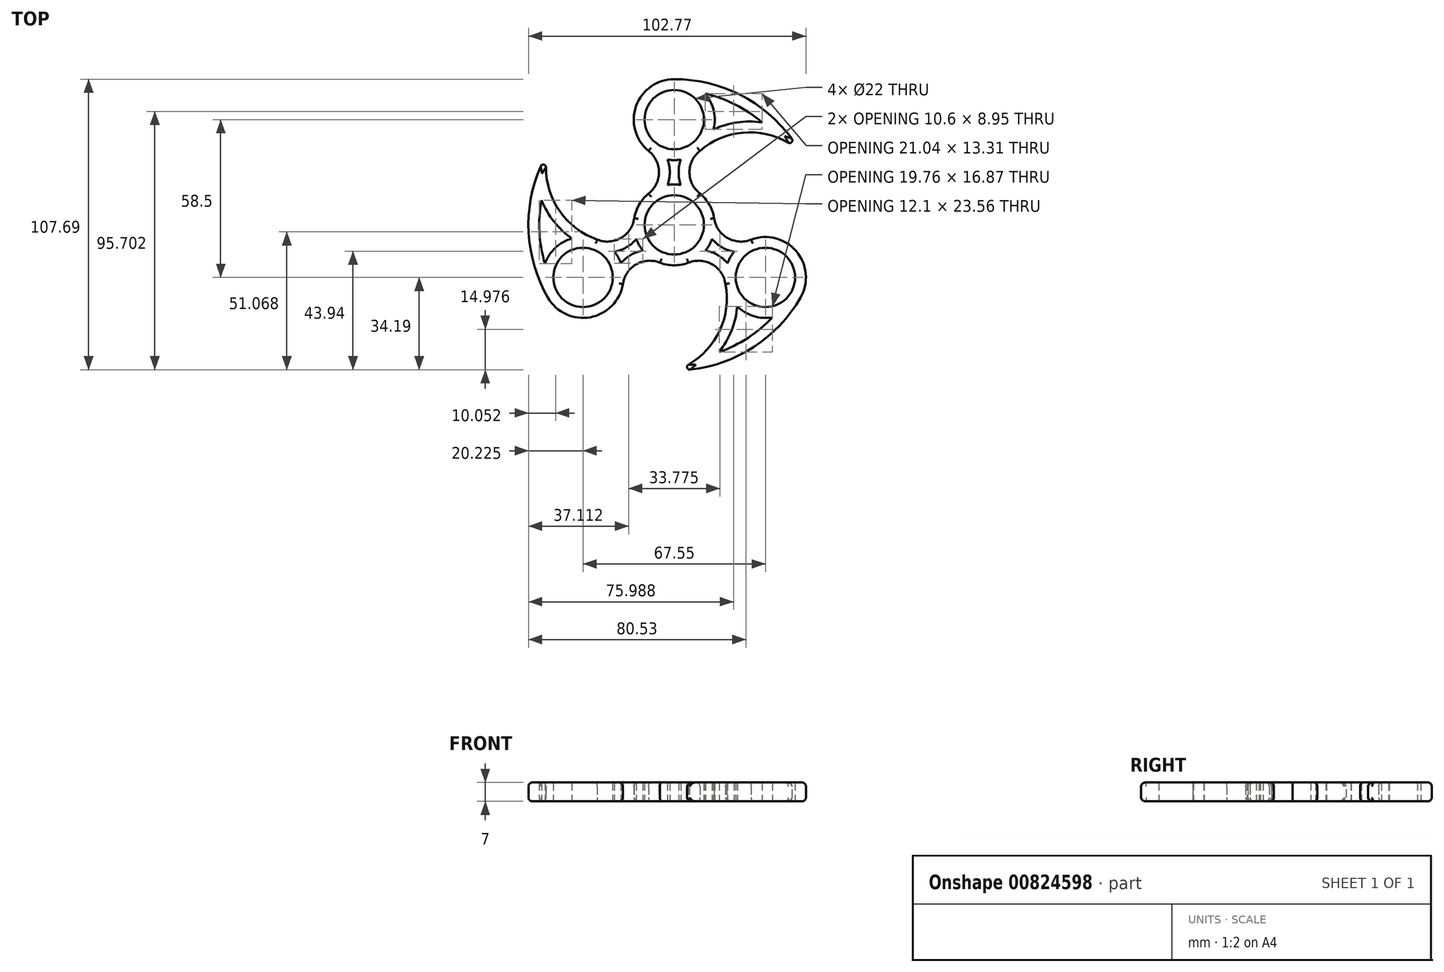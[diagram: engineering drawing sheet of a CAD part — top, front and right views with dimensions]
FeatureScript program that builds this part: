
annotation { "Feature Type Name" : "Feature", "Feature Type Description" : "" }
export const myFeature = defineFeature(function(context is Context, id is Id, definition is map)
    precondition{}
    {
        {
            var Q0;
            Q0=qCreatedBy(makeId("Top.planeOp"),FACE);
            var sketch = newSketch(context, id + "F0", { "sketchPlane" : qUnion([Q0])});
            skCircle(sketch, "E0", {"center": v(0, 0) * mm, "radius": 11 * mm});
            skCircle(sketch, "E1", {"center": v(0, 0) * mm, "radius": 15 * mm});
            skCircle(sketch, "E2", {"center": v(0, 39) * mm, "radius": 11 * mm});
            skCircle(sketch, "E3", {"center": v(0, 39) * mm, "radius": 15 * mm});
            skPoint(sketch, "E4", {"position": v(9.52, 27.4) * mm});
            skPoint(sketch, "E5", {"position": v(9.52, 11.6) * mm});
            skArc(sketch, "E6", {"start": v(9.52, 27.4) * mm, "mid": v(5.64, 19.5) * mm, "end": v(9.52, 11.6) * mm});
            skArc(sketch, "E7.MirrorCS", {"start": v(-9.52, 27.4) * mm, "mid": v(-5.64, 19.5) * mm, "end": v(-9.52, 11.6) * mm});
            skPoint(sketch, "E8", {"position": v(0, 54) * mm});
            skArc(sketch, "E9", {"start": v(46.53, 27.4) * mm, "mid": v(28.02, 34.3) * mm, "end": v(9.52, 27.4) * mm});
            skArc(sketch, "E10", {"start": v(46.53, 27.4) * mm, "mid": v(26.8, 46.88) * mm, "end": v(0, 54) * mm});
            skArc(sketch, "E11.0", {"start": v(32.5, 38) * mm, "mid": v(18.88, 36.98) * mm, "end": v(6.9, 30.43) * mm});
            skArc(sketch, "E11.1", {"start": v(32.5, 38) * mm, "mid": v(17.33, 46.9) * mm, "end": v(0, 50) * mm});
            skCircle(sketch, "E12.1.0", {"center": v(-33.77, -19.5) * mm, "radius": 11 * mm});
            skArc(sketch, "E12.1.1", {"start": v(-49.15, 9.16) * mm, "mid": v(-49.28, -8.45) * mm, "end": v(-43.3, -25) * mm});
            skArc(sketch, "E12.1.2", {"start": v(-49.15, 9.16) * mm, "mid": v(-41.47, -2.14) * mm, "end": v(-29.8, -9.24) * mm});
            skArc(sketch, "E12.1.3", {"start": v(-47, 26.6) * mm, "mid": v(-54, -0.23) * mm, "end": v(-46.77, -27) * mm});
            skArc(sketch, "E12.1.4", {"start": v(-47, 26.6) * mm, "mid": v(-43.72, 7.12) * mm, "end": v(-28.5, -5.46) * mm});
            skArc(sketch, "E12.1.5", {"start": v(-18.98, -21.94) * mm, "mid": v(-14.07, -14.64) * mm, "end": v(-5.28, -14.04) * mm});
            skArc(sketch, "E12.1.6", {"start": v(-28.5, -5.46) * mm, "mid": v(-19.7, -4.86) * mm, "end": v(-14.8, 2.44) * mm});
            skCircle(sketch, "E12.1.7", {"center": v(-33.77, -19.5) * mm, "radius": 15 * mm});
            skPoint(sketch, "E12.1.10", {"position": v(-46.77, -27) * mm});
            skPoint(sketch, "E12.1.11", {"position": v(-28.5, -5.46) * mm});
            skCircle(sketch, "E12.2.0", {"center": v(33.77, -19.5) * mm, "radius": 11 * mm});
            skArc(sketch, "E12.2.1", {"start": v(16.65, -47.15) * mm, "mid": v(31.95, -38.46) * mm, "end": v(43.3, -25) * mm});
            skArc(sketch, "E12.2.2", {"start": v(16.65, -47.15) * mm, "mid": v(22.59, -34.84) * mm, "end": v(22.9, -21.19) * mm});
            skArc(sketch, "E12.2.3", {"start": v(0.47, -54) * mm, "mid": v(27.2, -46.65) * mm, "end": v(46.77, -27) * mm});
            skArc(sketch, "E12.2.4", {"start": v(0.47, -54) * mm, "mid": v(15.7, -41.42) * mm, "end": v(18.98, -21.94) * mm});
            skArc(sketch, "E12.2.5", {"start": v(28.5, -5.46) * mm, "mid": v(19.7, -4.86) * mm, "end": v(14.8, 2.44) * mm});
            skArc(sketch, "E12.2.6", {"start": v(18.98, -21.94) * mm, "mid": v(14.07, -14.64) * mm, "end": v(5.28, -14.04) * mm});
            skCircle(sketch, "E12.2.7", {"center": v(33.77, -19.5) * mm, "radius": 15 * mm});
            skPoint(sketch, "E12.2.10", {"position": v(46.77, -27) * mm});
            skPoint(sketch, "E12.2.11", {"position": v(18.98, -21.94) * mm});
            skArc(sketch, "E13.0", {"start": v(7.07, 30.57) * mm, "mid": v(1.64, 19.5) * mm, "end": v(7.07, 8.43) * mm});
            skArc(sketch, "E14.0", {"start": v(-7.07, 30.57) * mm, "mid": v(-1.64, 19.5) * mm, "end": v(-7.07, 8.43) * mm});
            skArc(sketch, "E15.1.0", {"start": v(-22.94, -21.4) * mm, "mid": v(-16.07, -11.17) * mm, "end": v(-3.77, -10.34) * mm});
            skArc(sketch, "E15.1.1", {"start": v(-30, -9.16) * mm, "mid": v(-17.7, -8.33) * mm, "end": v(-10.84, 1.9) * mm});
            skArc(sketch, "E15.2.0", {"start": v(30, -9.16) * mm, "mid": v(17.7, -8.33) * mm, "end": v(10.84, 1.9) * mm});
            skArc(sketch, "E15.2.1", {"start": v(22.94, -21.4) * mm, "mid": v(16.07, -11.17) * mm, "end": v(3.77, -10.34) * mm});
            skSolve(sketch);
        }
        {
            var Q0;
            {var subQ0=sQuery(id+"F0.wireOp",EDGE,"E10");Q0=makeQuery(id+"F0.imprint","IMPRINT",FACE,{"disambiguationData":[TD([[makeQuery(id+"F0.imprint","IMPRINT",EDGE,{"derivedFrom":subQ0}),1.0]])]});}
            var Q1;
            {var subQ4=sQuery(id+"F0.wireOp",EDGE,"E11.1");var subQ7=sQuery(id+"F0.wireOp",EDGE,"E2");var subQ10=makeQuery(id+"F0.imprint","INTERSECT",VERTEX,{"derivedFrom":[subQ7,subQ4]});Q1=makeQuery(id+"F0.imprint","IMPRINT",FACE,{"disambiguationData":[TD([[makeQuery(id+"F0.imprint","IMPRINT",EDGE,{"disambiguationData":[TD([[subQ10,-1.0]])],"derivedFrom":subQ7}),-1.0]])]});}
            var Q2;
            {var subQ0=sQuery(id+"F0.wireOp",EDGE,"E11.1");var subQ1=sQuery(id+"F0.wireOp",EDGE,"E2");var subQ2=makeQuery(id+"F0.imprint","INTERSECT",VERTEX,{"derivedFrom":[subQ1,subQ0]});Q2=makeQuery(id+"F0.imprint","IMPRINT",FACE,{"disambiguationData":[TD([[makeQuery(id+"F0.imprint","IMPRINT",EDGE,{"disambiguationData":[TD([[subQ2,1.0]])],"derivedFrom":subQ1}),-1.0]])]});}
            var Q3;
            {var subQ5=sQuery(id+"F0.wireOp",EDGE,"E2");var subQ7=sQuery(id+"F0.wireOp",EDGE,"E11.0");var subQ10=makeQuery(id+"F0.imprint","INTERSECT",VERTEX,{"disambiguationData":[OD(0.0)],"derivedFrom":[subQ5,subQ7]});Q3=makeQuery(id+"F0.imprint","IMPRINT",FACE,{"disambiguationData":[TD([[makeQuery(id+"F0.imprint","IMPRINT",EDGE,{"disambiguationData":[TD([[subQ10,1.0]])],"derivedFrom":subQ5}),-1.0]])]});}
            var Q4;
            {var subQ0=sQuery(id+"F0.wireOp",EDGE,"E14.0");var subQ1=sQuery(id+"F0.wireOp",EDGE,"E2");var subQ2=makeQuery(id+"F0.imprint","INTERSECT",VERTEX,{"disambiguationData":[OD(1.0)],"derivedFrom":[subQ1,subQ0]});Q4=makeQuery(id+"F0.imprint","IMPRINT",FACE,{"disambiguationData":[TD([[makeQuery(id+"F0.imprint","IMPRINT",EDGE,{"disambiguationData":[TD([[subQ2,-1.0]])],"derivedFrom":subQ1}),-1.0]])]});}
            var Q5;
            {var subQ0=sQuery(id+"F0.wireOp",EDGE,"E6");var subQ1=sQuery(id+"F0.wireOp",EDGE,"E1");var subQ2=makeQuery(id+"F0.imprint","INTERSECT",VERTEX,{"disambiguationData":[OD(1.0)],"derivedFrom":[subQ1,subQ0]});Q5=makeQuery(id+"F0.imprint","IMPRINT",FACE,{"disambiguationData":[TD([[makeQuery(id+"F0.imprint","IMPRINT",EDGE,{"disambiguationData":[TD([[subQ2,-1.0]])],"derivedFrom":subQ1}),-1.0]])]});}
            var Q6;
            {var subQ0=sQuery(id+"F0.wireOp",EDGE,"E7.MirrorCS");var subQ1=sQuery(id+"F0.wireOp",EDGE,"E1");var subQ2=makeQuery(id+"F0.imprint","INTERSECT",VERTEX,{"disambiguationData":[OD(1.0)],"derivedFrom":[subQ1,subQ0]});Q6=makeQuery(id+"F0.imprint","IMPRINT",FACE,{"disambiguationData":[TD([[makeQuery(id+"F0.imprint","IMPRINT",EDGE,{"disambiguationData":[TD([[subQ2,1.0]])],"derivedFrom":subQ1}),-1.0]])]});}
            var Q7;
            {var subQ3=sQuery(id+"F0.wireOp",EDGE,"E14.0");var subQ6=sQuery(id+"F0.wireOp",EDGE,"E0");var subQ12=makeQuery(id+"F0.imprint","INTERSECT",VERTEX,{"disambiguationData":[OD(0.0)],"derivedFrom":[subQ6,subQ3]});Q7=makeQuery(id+"F0.imprint","IMPRINT",FACE,{"disambiguationData":[TD([[makeQuery(id+"F0.imprint","IMPRINT",EDGE,{"disambiguationData":[TD([[subQ12,1.0]])],"derivedFrom":subQ6}),-1.0]])]});}
            var Q8;
            {var subQ0=sQuery(id+"F0.wireOp",EDGE,"E15.1.1");var subQ1=sQuery(id+"F0.wireOp",EDGE,"E0");var subQ2=makeQuery(id+"F0.imprint","INTERSECT",VERTEX,{"disambiguationData":[OD(1.0)],"derivedFrom":[subQ1,subQ0]});Q8=makeQuery(id+"F0.imprint","IMPRINT",FACE,{"disambiguationData":[TD([[makeQuery(id+"F0.imprint","IMPRINT",EDGE,{"disambiguationData":[TD([[subQ2,-1.0]])],"derivedFrom":subQ1}),-1.0]])]});}
            var Q9;
            {var subQ1=sQuery(id+"F0.wireOp",EDGE,"E0");var subQ4=sQuery(id+"F0.wireOp",EDGE,"E15.1.0");var subQ5=makeQuery(id+"F0.imprint","INTERSECT",VERTEX,{"disambiguationData":[OD(0.0)],"derivedFrom":[subQ1,subQ4]});Q9=makeQuery(id+"F0.imprint","IMPRINT",FACE,{"disambiguationData":[TD([[makeQuery(id+"F0.imprint","IMPRINT",EDGE,{"disambiguationData":[TD([[subQ5,1.0]])],"derivedFrom":subQ1}),-1.0]])]});}
            var Q10;
            {var subQ0=sQuery(id+"F0.wireOp",EDGE,"E15.2.0");var subQ1=sQuery(id+"F0.wireOp",EDGE,"E0");var subQ2=makeQuery(id+"F0.imprint","INTERSECT",VERTEX,{"disambiguationData":[OD(1.0)],"derivedFrom":[subQ1,subQ0]});Q10=makeQuery(id+"F0.imprint","IMPRINT",FACE,{"disambiguationData":[TD([[makeQuery(id+"F0.imprint","IMPRINT",EDGE,{"disambiguationData":[TD([[subQ2,1.0]])],"derivedFrom":subQ1}),-1.0]])]});}
            var Q11;
            {var subQ6=sQuery(id+"F0.wireOp",EDGE,"E0");var subQ10=sQuery(id+"F0.wireOp",EDGE,"E15.2.0");var subQ11=makeQuery(id+"F0.imprint","INTERSECT",VERTEX,{"disambiguationData":[OD(0.0)],"derivedFrom":[subQ6,subQ10]});Q11=makeQuery(id+"F0.imprint","IMPRINT",FACE,{"disambiguationData":[TD([[makeQuery(id+"F0.imprint","IMPRINT",EDGE,{"disambiguationData":[TD([[subQ11,1.0]])],"derivedFrom":subQ6}),-1.0]])]});}
            var Q12;
            {var subQ0=sQuery(id+"F0.wireOp",EDGE,"E13.0");var subQ1=sQuery(id+"F0.wireOp",EDGE,"E0");var subQ2=makeQuery(id+"F0.imprint","INTERSECT",VERTEX,{"disambiguationData":[OD(1.0)],"derivedFrom":[subQ1,subQ0]});Q12=makeQuery(id+"F0.imprint","IMPRINT",FACE,{"disambiguationData":[TD([[makeQuery(id+"F0.imprint","IMPRINT",EDGE,{"disambiguationData":[TD([[subQ2,-1.0]])],"derivedFrom":subQ1}),-1.0]])]});}
            var Q13;
            {var subQ0=sQuery(id+"F0.wireOp",EDGE,"E12.2.5");var subQ1=sQuery(id+"F0.wireOp",EDGE,"E1");var subQ2=makeQuery(id+"F0.imprint","INTERSECT",VERTEX,{"disambiguationData":[OD(1.0)],"derivedFrom":[subQ1,subQ0]});Q13=makeQuery(id+"F0.imprint","IMPRINT",FACE,{"disambiguationData":[TD([[makeQuery(id+"F0.imprint","IMPRINT",EDGE,{"disambiguationData":[TD([[subQ2,1.0]])],"derivedFrom":subQ1}),-1.0]])]});}
            var Q14;
            {var subQ0=sQuery(id+"F0.wireOp",EDGE,"E12.2.6");var subQ1=sQuery(id+"F0.wireOp",EDGE,"E1");var subQ2=makeQuery(id+"F0.imprint","INTERSECT",VERTEX,{"disambiguationData":[OD(1.0)],"derivedFrom":[subQ1,subQ0]});Q14=makeQuery(id+"F0.imprint","IMPRINT",FACE,{"disambiguationData":[TD([[makeQuery(id+"F0.imprint","IMPRINT",EDGE,{"disambiguationData":[TD([[subQ2,-1.0]])],"derivedFrom":subQ1}),-1.0]])]});}
            var Q15;
            {var subQ0=sQuery(id+"F0.wireOp",EDGE,"E12.2.2");var subQ1=sQuery(id+"F0.wireOp",EDGE,"E12.2.0");var subQ10=makeQuery(id+"F0.imprint","INTERSECT",VERTEX,{"disambiguationData":[OD(0.0)],"derivedFrom":[subQ1,subQ0]});Q15=makeQuery(id+"F0.imprint","IMPRINT",FACE,{"disambiguationData":[TD([[makeQuery(id+"F0.imprint","IMPRINT",EDGE,{"disambiguationData":[TD([[subQ10,1.0]])],"derivedFrom":subQ1}),-1.0]])]});}
            var Q16;
            {var subQ0=sQuery(id+"F0.wireOp",EDGE,"E12.2.3");Q16=makeQuery(id+"F0.imprint","IMPRINT",FACE,{"disambiguationData":[TD([[makeQuery(id+"F0.imprint","IMPRINT",EDGE,{"derivedFrom":subQ0}),1.0]])]});}
            var Q17;
            {var subQ0=sQuery(id+"F0.wireOp",EDGE,"E12.2.1");var subQ1=sQuery(id+"F0.wireOp",EDGE,"E12.2.0");var subQ2=makeQuery(id+"F0.imprint","INTERSECT",VERTEX,{"derivedFrom":[subQ1,subQ0]});Q17=makeQuery(id+"F0.imprint","IMPRINT",FACE,{"disambiguationData":[TD([[makeQuery(id+"F0.imprint","IMPRINT",EDGE,{"disambiguationData":[TD([[subQ2,1.0]])],"derivedFrom":subQ1}),-1.0]])]});}
            var Q18;
            {var subQ0=sQuery(id+"F0.wireOp",EDGE,"E12.2.1");var subQ1=sQuery(id+"F0.wireOp",EDGE,"E12.2.0");var subQ2=makeQuery(id+"F0.imprint","INTERSECT",VERTEX,{"derivedFrom":[subQ1,subQ0]});Q18=makeQuery(id+"F0.imprint","IMPRINT",FACE,{"disambiguationData":[TD([[makeQuery(id+"F0.imprint","IMPRINT",EDGE,{"disambiguationData":[TD([[subQ2,-1.0]])],"derivedFrom":subQ1}),-1.0]])]});}
            var Q19;
            {var subQ0=sQuery(id+"F0.wireOp",EDGE,"E15.2.0");var subQ1=sQuery(id+"F0.wireOp",EDGE,"E12.2.0");var subQ2=makeQuery(id+"F0.imprint","INTERSECT",VERTEX,{"disambiguationData":[OD(1.0)],"derivedFrom":[subQ1,subQ0]});Q19=makeQuery(id+"F0.imprint","IMPRINT",FACE,{"disambiguationData":[TD([[makeQuery(id+"F0.imprint","IMPRINT",EDGE,{"disambiguationData":[TD([[subQ2,-1.0]])],"derivedFrom":subQ1}),-1.0]])]});}
            var Q20;
            {var subQ0=sQuery(id+"F0.wireOp",EDGE,"E12.1.5");var subQ1=sQuery(id+"F0.wireOp",EDGE,"E1");var subQ2=makeQuery(id+"F0.imprint","INTERSECT",VERTEX,{"disambiguationData":[OD(1.0)],"derivedFrom":[subQ1,subQ0]});Q20=makeQuery(id+"F0.imprint","IMPRINT",FACE,{"disambiguationData":[TD([[makeQuery(id+"F0.imprint","IMPRINT",EDGE,{"disambiguationData":[TD([[subQ2,1.0]])],"derivedFrom":subQ1}),-1.0]])]});}
            var Q21;
            {var subQ0=sQuery(id+"F0.wireOp",EDGE,"E12.1.6");var subQ1=sQuery(id+"F0.wireOp",EDGE,"E1");var subQ2=makeQuery(id+"F0.imprint","INTERSECT",VERTEX,{"disambiguationData":[OD(1.0)],"derivedFrom":[subQ1,subQ0]});Q21=makeQuery(id+"F0.imprint","IMPRINT",FACE,{"disambiguationData":[TD([[makeQuery(id+"F0.imprint","IMPRINT",EDGE,{"disambiguationData":[TD([[subQ2,-1.0]])],"derivedFrom":subQ1}),-1.0]])]});}
            var Q22;
            {var subQ0=sQuery(id+"F0.wireOp",EDGE,"E12.1.2");var subQ1=sQuery(id+"F0.wireOp",EDGE,"E12.1.0");var subQ11=makeQuery(id+"F0.imprint","INTERSECT",VERTEX,{"disambiguationData":[OD(0.0)],"derivedFrom":[subQ1,subQ0]});Q22=makeQuery(id+"F0.imprint","IMPRINT",FACE,{"disambiguationData":[TD([[makeQuery(id+"F0.imprint","IMPRINT",EDGE,{"disambiguationData":[TD([[subQ11,1.0]])],"derivedFrom":subQ1}),-1.0]])]});}
            var Q23;
            {var subQ0=sQuery(id+"F0.wireOp",EDGE,"E15.1.0");var subQ1=sQuery(id+"F0.wireOp",EDGE,"E12.1.0");var subQ2=makeQuery(id+"F0.imprint","INTERSECT",VERTEX,{"disambiguationData":[OD(1.0)],"derivedFrom":[subQ1,subQ0]});Q23=makeQuery(id+"F0.imprint","IMPRINT",FACE,{"disambiguationData":[TD([[makeQuery(id+"F0.imprint","IMPRINT",EDGE,{"disambiguationData":[TD([[subQ2,-1.0]])],"derivedFrom":subQ1}),-1.0]])]});}
            var Q24;
            {var subQ0=sQuery(id+"F0.wireOp",EDGE,"E12.1.1");var subQ1=sQuery(id+"F0.wireOp",EDGE,"E12.1.0");var subQ2=makeQuery(id+"F0.imprint","INTERSECT",VERTEX,{"derivedFrom":[subQ1,subQ0]});Q24=makeQuery(id+"F0.imprint","IMPRINT",FACE,{"disambiguationData":[TD([[makeQuery(id+"F0.imprint","IMPRINT",EDGE,{"disambiguationData":[TD([[subQ2,-1.0]])],"derivedFrom":subQ1}),-1.0]])]});}
            var Q25;
            {var subQ0=sQuery(id+"F0.wireOp",EDGE,"E12.1.1");var subQ1=sQuery(id+"F0.wireOp",EDGE,"E12.1.0");var subQ2=makeQuery(id+"F0.imprint","INTERSECT",VERTEX,{"derivedFrom":[subQ1,subQ0]});Q25=makeQuery(id+"F0.imprint","IMPRINT",FACE,{"disambiguationData":[TD([[makeQuery(id+"F0.imprint","IMPRINT",EDGE,{"disambiguationData":[TD([[subQ2,1.0]])],"derivedFrom":subQ1}),-1.0]])]});}
            var Q26;
            {var subQ0=sQuery(id+"F0.wireOp",EDGE,"E12.1.3");Q26=makeQuery(id+"F0.imprint","IMPRINT",FACE,{"disambiguationData":[TD([[makeQuery(id+"F0.imprint","IMPRINT",EDGE,{"derivedFrom":subQ0}),1.0]])]});}
            extrude(context, id + "F1", {"entities" : qUnion([Q0, Q1, Q2, Q3, Q4, Q5, Q6, Q7, Q8, Q9, Q10, Q11, Q12, Q13, Q14, Q15, Q16, Q17, Q18, Q19, Q20, Q21, Q22, Q23, Q24, Q25, Q26]), "depth" : 7 * mm, "offsetDistance" : 25 * mm});
        }
        {
            var Q0;
            Q0=makeQuery(id+"F1.opExtrude","CAP_EDGE",EDGE,{"disambiguationData":[OSD([sQuery(id+"F0.wireOp",EDGE,"E10")])],"isStart":false});
            var Q1;
            {var subQ0=sQuery(id+"F0.wireOp",EDGE,"E3");Q1=makeQuery(id+"F1.opExtrude","CAP_EDGE",EDGE,{"disambiguationData":[OSD([subQ0]),TDD([makeQuery(id+"F0.imprint","IMPRINT",EDGE,{"disambiguationData":[TD([[makeQuery(id+"F0.imprint","INTERSECT",VERTEX,{"disambiguationData":[OD(0.0)],"derivedFrom":[subQ0,sQuery(id+"F0.wireOp",EDGE,"E7.MirrorCS")]}),1.0]])],"derivedFrom":subQ0})])],"isStart":false});}
            var Q2;
            Q2=makeQuery(id+"F1.opExtrude","CAP_EDGE",EDGE,{"disambiguationData":[OSD([sQuery(id+"F0.wireOp",EDGE,"E7.MirrorCS")])],"isStart":false});
            var Q3;
            {var subQ0=sQuery(id+"F0.wireOp",EDGE,"E1");Q3=makeQuery(id+"F1.opExtrude","CAP_EDGE",EDGE,{"disambiguationData":[OSD([subQ0]),TDD([makeQuery(id+"F0.imprint","IMPRINT",EDGE,{"disambiguationData":[TD([[makeQuery(id+"F0.imprint","INTERSECT",VERTEX,{"disambiguationData":[OD(0.0)],"derivedFrom":[subQ0,sQuery(id+"F0.wireOp",EDGE,"E7.MirrorCS")]}),-1.0]])],"derivedFrom":subQ0})])],"isStart":false});}
            var Q4;
            Q4=makeQuery(id+"F1.opExtrude","CAP_EDGE",EDGE,{"disambiguationData":[OSD([sQuery(id+"F0.wireOp",EDGE,"E12.1.6")])],"isStart":false});
            var Q5;
            Q5=makeQuery(id+"F1.opExtrude","CAP_EDGE",EDGE,{"disambiguationData":[OSD([sQuery(id+"F0.wireOp",EDGE,"E12.1.4")])],"isStart":false});
            var Q6;
            Q6=makeQuery(id+"F1.opExtrude","CAP_EDGE",EDGE,{"disambiguationData":[OSD([sQuery(id+"F0.wireOp",EDGE,"E12.1.3")])],"isStart":false});
            var Q7;
            {var subQ0=sQuery(id+"F0.wireOp",EDGE,"E12.1.7");Q7=makeQuery(id+"F1.opExtrude","CAP_EDGE",EDGE,{"disambiguationData":[OSD([subQ0]),TDD([makeQuery(id+"F0.imprint","IMPRINT",EDGE,{"disambiguationData":[TD([[makeQuery(id+"F0.imprint","INTERSECT",VERTEX,{"derivedFrom":[sQuery(id+"F0.wireOp",EDGE,"E12.1.3"),subQ0]}),-1.0]])],"derivedFrom":subQ0})])],"isStart":false});}
            var Q8;
            Q8=makeQuery(id+"F1.opExtrude","CAP_EDGE",EDGE,{"disambiguationData":[OSD([sQuery(id+"F0.wireOp",EDGE,"E12.1.5")])],"isStart":false});
            var Q9;
            {var subQ0=sQuery(id+"F0.wireOp",EDGE,"E1");Q9=makeQuery(id+"F1.opExtrude","CAP_EDGE",EDGE,{"disambiguationData":[OSD([subQ0]),TDD([makeQuery(id+"F0.imprint","IMPRINT",EDGE,{"disambiguationData":[TD([[makeQuery(id+"F0.imprint","INTERSECT",VERTEX,{"disambiguationData":[OD(0.0)],"derivedFrom":[subQ0,sQuery(id+"F0.wireOp",EDGE,"E12.1.5")]}),-1.0]])],"derivedFrom":subQ0})])],"isStart":false});}
            var Q10;
            Q10=makeQuery(id+"F1.opExtrude","CAP_EDGE",EDGE,{"disambiguationData":[OSD([sQuery(id+"F0.wireOp",EDGE,"E12.2.6")])],"isStart":false});
            var Q11;
            Q11=makeQuery(id+"F1.opExtrude","CAP_EDGE",EDGE,{"disambiguationData":[OSD([sQuery(id+"F0.wireOp",EDGE,"E12.2.4")])],"isStart":false});
            var Q12;
            Q12=makeQuery(id+"F1.opExtrude","CAP_EDGE",EDGE,{"disambiguationData":[OSD([sQuery(id+"F0.wireOp",EDGE,"E12.2.3")])],"isStart":false});
            var Q13;
            {var subQ0=sQuery(id+"F0.wireOp",EDGE,"E12.2.7");Q13=makeQuery(id+"F1.opExtrude","CAP_EDGE",EDGE,{"disambiguationData":[OSD([subQ0]),TDD([makeQuery(id+"F0.imprint","IMPRINT",EDGE,{"disambiguationData":[TD([[makeQuery(id+"F0.imprint","INTERSECT",VERTEX,{"derivedFrom":[sQuery(id+"F0.wireOp",EDGE,"E12.2.3"),subQ0]}),-1.0]])],"derivedFrom":subQ0})])],"isStart":false});}
            var Q14;
            Q14=makeQuery(id+"F1.opExtrude","CAP_EDGE",EDGE,{"disambiguationData":[OSD([sQuery(id+"F0.wireOp",EDGE,"E12.2.5")])],"isStart":false});
            var Q15;
            {var subQ0=sQuery(id+"F0.wireOp",EDGE,"E1");Q15=makeQuery(id+"F1.opExtrude","CAP_EDGE",EDGE,{"disambiguationData":[OSD([subQ0]),TDD([makeQuery(id+"F0.imprint","IMPRINT",EDGE,{"disambiguationData":[TD([[makeQuery(id+"F0.imprint","INTERSECT",VERTEX,{"disambiguationData":[OD(0.0)],"derivedFrom":[subQ0,sQuery(id+"F0.wireOp",EDGE,"E6")]}),1.0]])],"derivedFrom":subQ0})])],"isStart":false});}
            var Q16;
            Q16=makeQuery(id+"F1.opExtrude","CAP_EDGE",EDGE,{"disambiguationData":[OSD([sQuery(id+"F0.wireOp",EDGE,"E6")])],"isStart":false});
            var Q17;
            Q17=makeQuery(id+"F1.opExtrude","CAP_EDGE",EDGE,{"disambiguationData":[OSD([sQuery(id+"F0.wireOp",EDGE,"E9")])],"isStart":false});
            fillet(context, id + "F2", {"entities" : qUnion([Q0, Q1, Q2, Q3, Q4, Q5, Q6, Q7, Q8, Q9, Q10, Q11, Q12, Q13, Q14, Q15, Q16, Q17]), "radius" : 1.5 * mm, "tangentPropagation" : true, "allowEdgeOverflow" : false});
        }
        {
            var Q0;
            {var subQ0=sQuery(id+"F0.wireOp",EDGE,"E12.2.7");Q0=makeQuery(id+"F1.opExtrude","CAP_EDGE",EDGE,{"disambiguationData":[OSD([subQ0]),TDD([makeQuery(id+"F0.imprint","IMPRINT",EDGE,{"disambiguationData":[TD([[makeQuery(id+"F0.imprint","INTERSECT",VERTEX,{"derivedFrom":[sQuery(id+"F0.wireOp",EDGE,"E12.2.3"),subQ0]}),-1.0]])],"derivedFrom":subQ0})])],"isStart":true});}
            var Q1;
            Q1=makeQuery(id+"F1.opExtrude","CAP_EDGE",EDGE,{"disambiguationData":[OSD([sQuery(id+"F0.wireOp",EDGE,"E12.2.3")])],"isStart":true});
            var Q2;
            Q2=makeQuery(id+"F1.opExtrude","CAP_EDGE",EDGE,{"disambiguationData":[OSD([sQuery(id+"F0.wireOp",EDGE,"E12.2.4")])],"isStart":true});
            var Q3;
            Q3=makeQuery(id+"F1.opExtrude","CAP_EDGE",EDGE,{"disambiguationData":[OSD([sQuery(id+"F0.wireOp",EDGE,"E12.2.6")])],"isStart":true});
            var Q4;
            {var subQ0=sQuery(id+"F0.wireOp",EDGE,"E1");Q4=makeQuery(id+"F1.opExtrude","CAP_EDGE",EDGE,{"disambiguationData":[OSD([subQ0]),TDD([makeQuery(id+"F0.imprint","IMPRINT",EDGE,{"disambiguationData":[TD([[makeQuery(id+"F0.imprint","INTERSECT",VERTEX,{"disambiguationData":[OD(0.0)],"derivedFrom":[subQ0,sQuery(id+"F0.wireOp",EDGE,"E6")]}),1.0]])],"derivedFrom":subQ0})])],"isStart":true});}
            var Q5;
            Q5=makeQuery(id+"F1.opExtrude","CAP_EDGE",EDGE,{"disambiguationData":[OSD([sQuery(id+"F0.wireOp",EDGE,"E12.2.5")])],"isStart":true});
            var Q6;
            Q6=makeQuery(id+"F1.opExtrude","CAP_EDGE",EDGE,{"disambiguationData":[OSD([sQuery(id+"F0.wireOp",EDGE,"E6")])],"isStart":true});
            var Q7;
            Q7=makeQuery(id+"F1.opExtrude","CAP_EDGE",EDGE,{"disambiguationData":[OSD([sQuery(id+"F0.wireOp",EDGE,"E9")])],"isStart":true});
            var Q8;
            Q8=makeQuery(id+"F1.opExtrude","CAP_EDGE",EDGE,{"disambiguationData":[OSD([sQuery(id+"F0.wireOp",EDGE,"E10")])],"isStart":true});
            var Q9;
            {var subQ0=sQuery(id+"F0.wireOp",EDGE,"E3");Q9=makeQuery(id+"F1.opExtrude","CAP_EDGE",EDGE,{"disambiguationData":[OSD([subQ0]),TDD([makeQuery(id+"F0.imprint","IMPRINT",EDGE,{"disambiguationData":[TD([[makeQuery(id+"F0.imprint","INTERSECT",VERTEX,{"disambiguationData":[OD(0.0)],"derivedFrom":[subQ0,sQuery(id+"F0.wireOp",EDGE,"E7.MirrorCS")]}),1.0]])],"derivedFrom":subQ0})])],"isStart":true});}
            var Q10;
            Q10=makeQuery(id+"F1.opExtrude","CAP_EDGE",EDGE,{"disambiguationData":[OSD([sQuery(id+"F0.wireOp",EDGE,"E7.MirrorCS")])],"isStart":true});
            var Q11;
            {var subQ0=sQuery(id+"F0.wireOp",EDGE,"E1");Q11=makeQuery(id+"F1.opExtrude","CAP_EDGE",EDGE,{"disambiguationData":[OSD([subQ0]),TDD([makeQuery(id+"F0.imprint","IMPRINT",EDGE,{"disambiguationData":[TD([[makeQuery(id+"F0.imprint","INTERSECT",VERTEX,{"disambiguationData":[OD(0.0)],"derivedFrom":[subQ0,sQuery(id+"F0.wireOp",EDGE,"E7.MirrorCS")]}),-1.0]])],"derivedFrom":subQ0})])],"isStart":true});}
            var Q12;
            Q12=makeQuery(id+"F1.opExtrude","CAP_EDGE",EDGE,{"disambiguationData":[OSD([sQuery(id+"F0.wireOp",EDGE,"E12.1.6")])],"isStart":true});
            var Q13;
            Q13=makeQuery(id+"F1.opExtrude","CAP_EDGE",EDGE,{"disambiguationData":[OSD([sQuery(id+"F0.wireOp",EDGE,"E12.1.4")])],"isStart":true});
            var Q14;
            Q14=makeQuery(id+"F1.opExtrude","CAP_EDGE",EDGE,{"disambiguationData":[OSD([sQuery(id+"F0.wireOp",EDGE,"E12.1.3")])],"isStart":true});
            var Q15;
            {var subQ0=sQuery(id+"F0.wireOp",EDGE,"E12.1.7");Q15=makeQuery(id+"F1.opExtrude","CAP_EDGE",EDGE,{"disambiguationData":[OSD([subQ0]),TDD([makeQuery(id+"F0.imprint","IMPRINT",EDGE,{"disambiguationData":[TD([[makeQuery(id+"F0.imprint","INTERSECT",VERTEX,{"derivedFrom":[sQuery(id+"F0.wireOp",EDGE,"E12.1.3"),subQ0]}),-1.0]])],"derivedFrom":subQ0})])],"isStart":true});}
            var Q16;
            Q16=makeQuery(id+"F1.opExtrude","CAP_EDGE",EDGE,{"disambiguationData":[OSD([sQuery(id+"F0.wireOp",EDGE,"E12.1.5")])],"isStart":true});
            var Q17;
            {var subQ0=sQuery(id+"F0.wireOp",EDGE,"E1");Q17=makeQuery(id+"F1.opExtrude","CAP_EDGE",EDGE,{"disambiguationData":[OSD([subQ0]),TDD([makeQuery(id+"F0.imprint","IMPRINT",EDGE,{"disambiguationData":[TD([[makeQuery(id+"F0.imprint","INTERSECT",VERTEX,{"disambiguationData":[OD(0.0)],"derivedFrom":[subQ0,sQuery(id+"F0.wireOp",EDGE,"E12.1.5")]}),-1.0]])],"derivedFrom":subQ0})])],"isStart":true});}
            fillet(context, id + "F3", {"entities" : qUnion([Q0, Q1, Q2, Q3, Q4, Q5, Q6, Q7, Q8, Q9, Q10, Q11, Q12, Q13, Q14, Q15, Q16, Q17]), "radius" : 1.5 * mm, "tangentPropagation" : true, "allowEdgeOverflow" : false});
        }
        {
            var Q0;
            Q0=makeQuery(id+"F1.opExtrude","SWEPT_EDGE",EDGE,{"disambiguationData":[OSD([sQuery(id+"F0.wireOp",EDGE,"E9"),sQuery(id+"F0.wireOp",EDGE,"E10")])]});
            var Q1;
            Q1=makeQuery(id+"F1.opExtrude","SWEPT_EDGE",EDGE,{"disambiguationData":[OSD([sQuery(id+"F0.wireOp",EDGE,"E12.2.3"),sQuery(id+"F0.wireOp",EDGE,"E12.2.4")])]});
            var Q2;
            Q2=makeQuery(id+"F1.opExtrude","SWEPT_EDGE",EDGE,{"disambiguationData":[OSD([sQuery(id+"F0.wireOp",EDGE,"E12.1.3"),sQuery(id+"F0.wireOp",EDGE,"E12.1.4")])]});
            fillet(context, id + "F4", {"entities" : qUnion([Q0, Q1, Q2]), "radius" : 1 * mm, "tangentPropagation" : true, "allowEdgeOverflow" : false});
        }
    });
